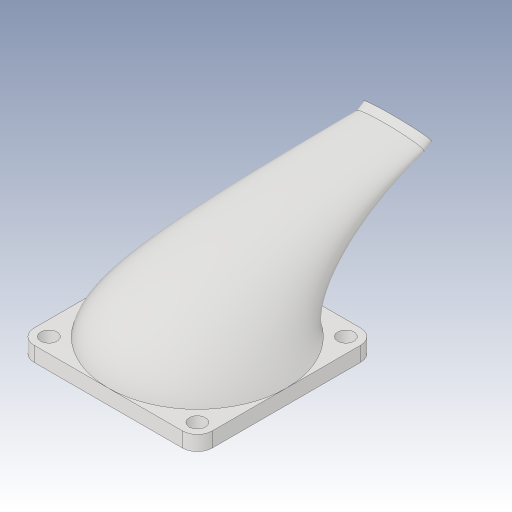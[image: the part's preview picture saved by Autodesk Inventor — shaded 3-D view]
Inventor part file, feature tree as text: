
AUTODESK INVENTOR PART (.ipt)
format: ipt  version: 2023.3 (Build 273359000, 359)  size: 412,160 bytes
history: native  units: in
note: dims shown in document units (in); Inventor stores cm internally (conversion verified against a paired STEP export)
features: sketch x5, plane x3, loft x2, extrude x1, sweep x1, projected_geometry x1
ambient origin geometry x8: Origin, YZ Plane, XZ Plane, XY Plane, X Axis, Y Axis, Z Axis, Center Point
bodies: Body1 (feature_tree)
feature tree (13):
  sketch  "Skizze3"  dims[d4=0.9449in d5=0.7874in]
  extrude  "Extrusion3"  Depth=0.7874in
  plane  "Arbeitsebene1"
  sketch  "Skizze6"  dims[d13=0.0787in d14=0.0in d15=0.5512in]
  plane  "Arbeitsebene3"
  sketch  "Skizze4"  dims[d6=0.1575in d7=0.0866in]
  plane  "Arbeitsebene2"
  sketch  "Skizze5"  dims[d8=1.5748in d10=360.0deg d12=0.8661in]
  loft  "Erhebung4"
  loft  "Erhebung5"
  sweep  "Sweeping1"
  projected_geometry  "Projizierte Kontur1"
  sketch  "Skizze8"  dims[d16=0.1575in d17=0.0394in d19=0.1772in d20=0.0551in d39=0.4331in d40=-0.2061in d41=0.0in d42=90.0deg d43=0.0in d44=90.0deg d45=0.0in d46=90.0deg d47=0.0in d48=90.0deg d49=0.0in d50=90.0deg d51=0.0in d52=90.0deg d53=0.0in d54=90.0deg d55=0.0in d56=90.0deg d57=0.4331in d58=0.1378in d63=0.5841in d65=0.0394in d66=0.0in d67=0.0in]
